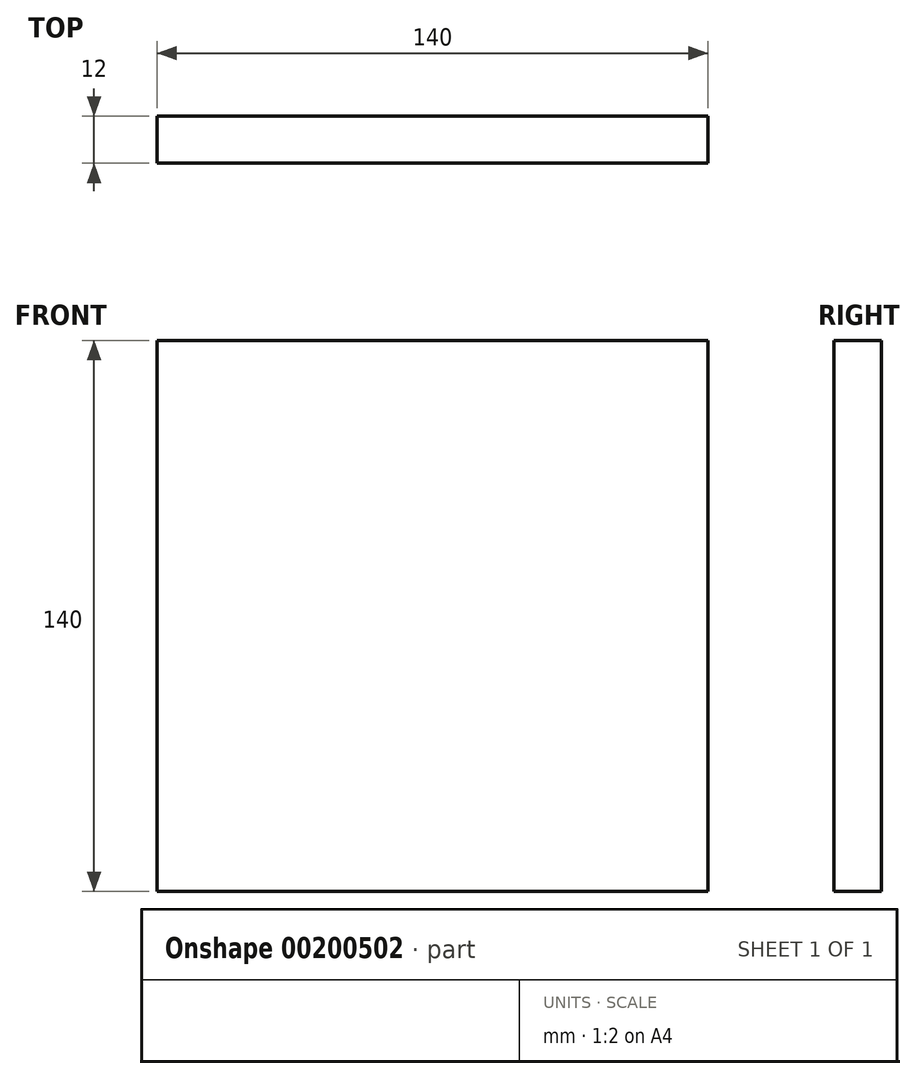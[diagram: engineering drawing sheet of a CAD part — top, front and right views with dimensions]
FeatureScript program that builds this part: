
annotation { "Feature Type Name" : "Feature", "Feature Type Description" : "" }
export const myFeature = defineFeature(function(context is Context, id is Id, definition is map)
    precondition{}
    {
        {
            var Q0;
            Q0=qCreatedBy(makeId("Front.planeOp"),FACE);
            var sketch = newSketch(context, id + "F0", { "sketchPlane" : qUnion([Q0])});
            skPoint(sketch, "E0.middle", {"position": v(0, 0) * mm});
            skLineSegment(sketch, "E1.bottom", {"start": v(70, 70) * mm, "end": v(-70, 70) * mm});
            skLineSegment(sketch, "E1.top", {"start": v(70, -70) * mm, "end": v(-70, -70) * mm});
            skLineSegment(sketch, "E1.left", {"start": v(70, 70) * mm, "end": v(70, -70) * mm});
            skLineSegment(sketch, "E1.right", {"start": v(-70, 70) * mm, "end": v(-70, -70) * mm});
            skSolve(sketch);
        }
        {
            var Q0;
            Q0=makeQuery(id+"F0.imprint","IMPRINT",FACE,{"disambiguationData":[TD([[makeQuery(id+"F0.imprint","IMPRINT",EDGE,{"derivedFrom":sQuery(id+"F0.wireOp",EDGE,"E1.bottom")}),1.0]])]});
            extrude(context, id + "F1", {"entities" : qUnion([Q0]), "depth" : 12 * mm});
        }
    });
